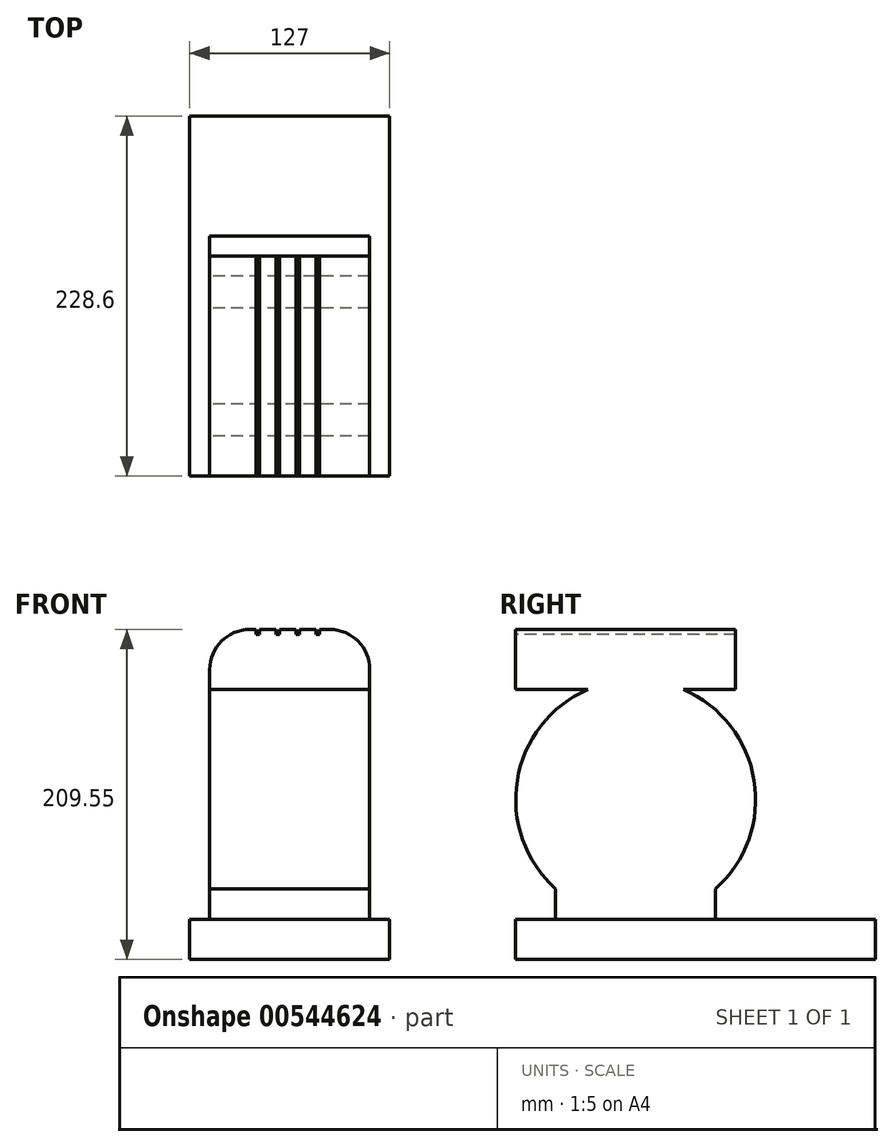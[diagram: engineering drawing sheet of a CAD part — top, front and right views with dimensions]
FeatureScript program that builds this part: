
annotation { "Feature Type Name" : "Feature", "Feature Type Description" : "" }
export const myFeature = defineFeature(function(context is Context, id is Id, definition is map)
    precondition{}
    {
        {
            var Q0;
            Q0=qCreatedBy(makeId("Right.planeOp"),FACE);
            var sketch = newSketch(context, id + "F0", { "sketchPlane" : qUnion([Q0])});
            skLineSegment(sketch, "E0.bottom", {"start": v(0, 0) * mm, "end": v(228.6, 0) * mm});
            skLineSegment(sketch, "E0.top", {"start": v(0, 25.4) * mm, "end": v(228.6, 25.4) * mm});
            skLineSegment(sketch, "E0.left", {"start": v(0, 0) * mm, "end": v(0, 25.4) * mm});
            skLineSegment(sketch, "E0.right", {"start": v(228.6, 0) * mm, "end": v(228.6, 25.4) * mm});
            skSolve(sketch);
        }
        {
            var Q0;
            Q0 = qSketchRegion(id + "F0", true);
            extrude(context, id + "F1", {"entities" : qUnion([Q0]), "endBound" : BoundingType.SYMMETRIC, "depth" : 127 * mm, "offsetDistance" : 25.4 * mm});
        }
        {
            var Q0;
            Q0=qCreatedBy(makeId("Right.planeOp"),FACE);
            var sketch = newSketch(context, id + "F2", { "sketchPlane" : qUnion([Q0])});
            skArc(sketch, "E1", {"start": v(127, 44.8) * mm, "mid": v(76.2, 177.8) * mm, "end": v(25.4, 44.8) * mm});
            skLineSegment(sketch, "E2", {"start": v(127, 44.8) * mm, "end": v(127, 6.35) * mm});
            skLineSegment(sketch, "E3", {"start": v(25.4, 44.8) * mm, "end": v(25.4, 6.35) * mm});
            skLineSegment(sketch, "E4", {"start": v(127, 6.35) * mm, "end": v(25.4, 6.35) * mm});
            skSolve(sketch);
        }
        {
            var Q0;
            Q0 = qSketchRegion(id + "F2", true);
            extrude(context, id + "F3", {"entities" : qUnion([Q0]), "operationType" : NewBodyOperationType.ADD, "endBound" : BoundingType.SYMMETRIC, "depth" : 101.6 * mm, "offsetDistance" : 25.4 * mm});
        }
        {
            var Q0;
            Q0=qCreatedBy(makeId("Front.planeOp"),FACE);
            var sketch = newSketch(context, id + "F4", { "sketchPlane" : qUnion([Q0])});
            skLineSegment(sketch, "E5", {"start": v(-50.8, 171.45) * mm, "end": v(50.8, 171.45) * mm});
            skLineSegment(sketch, "E6", {"start": v(0, 345.73) * mm, "end": v(0, 0) * mm, "construction": true});
            skLineSegment(sketch, "E7", {"start": v(-50.8, 171.45) * mm, "end": v(-50.8, 184.15) * mm});
            skLineSegment(sketch, "E8", {"start": v(50.8, 171.45) * mm, "end": v(50.8, 184.15) * mm});
            skLineSegment(sketch, "E9", {"start": v(-25.4, 209.55) * mm, "end": v(-21.57, 209.55) * mm});
            skPoint(sketch, "E10.visualSharp", {"position": v(-50.8, 209.55) * mm});
            skArc(sketch, "E10.filletArc", {"start": v(-25.4, 209.55) * mm, "mid": v(-43.36, 202.11) * mm, "end": v(-50.8, 184.15) * mm});
            skPoint(sketch, "E11.visualSharp", {"position": v(50.8, 209.55) * mm});
            skArc(sketch, "E11.filletArc", {"start": v(50.8, 184.15) * mm, "mid": v(43.36, 202.11) * mm, "end": v(25.4, 209.55) * mm});
            skLineSegment(sketch, "E12.top", {"start": v(18.87, 206.38) * mm, "end": v(16.53, 206.38) * mm});
            skLineSegment(sketch, "E12.left", {"start": v(18.87, 209.55) * mm, "end": v(18.87, 206.38) * mm});
            skLineSegment(sketch, "E12.right", {"start": v(16.53, 209.55) * mm, "end": v(16.53, 206.38) * mm});
            skLineSegment(sketch, "E13.top", {"start": v(6.17, 206.38) * mm, "end": v(3.83, 206.38) * mm});
            skLineSegment(sketch, "E13.left", {"start": v(6.17, 209.55) * mm, "end": v(6.17, 206.38) * mm});
            skLineSegment(sketch, "E13.right", {"start": v(3.83, 209.55) * mm, "end": v(3.83, 206.38) * mm});
            skLineSegment(sketch, "E14.top", {"start": v(-6.53, 206.38) * mm, "end": v(-8.87, 206.38) * mm});
            skLineSegment(sketch, "E14.left", {"start": v(-6.53, 209.55) * mm, "end": v(-6.53, 206.38) * mm});
            skLineSegment(sketch, "E14.right", {"start": v(-8.87, 209.55) * mm, "end": v(-8.87, 206.38) * mm});
            skLineSegment(sketch, "E15.top", {"start": v(-19.23, 206.38) * mm, "end": v(-21.57, 206.38) * mm});
            skLineSegment(sketch, "E15.left", {"start": v(-19.23, 209.55) * mm, "end": v(-19.23, 206.38) * mm});
            skLineSegment(sketch, "E15.right", {"start": v(-21.57, 209.55) * mm, "end": v(-21.57, 206.38) * mm});
            skLineSegment(sketch, "E16.trimOffspring", {"start": v(18.87, 209.55) * mm, "end": v(25.4, 209.55) * mm});
            skLineSegment(sketch, "E17.trimOffspring", {"start": v(6.17, 209.55) * mm, "end": v(16.53, 209.55) * mm});
            skLineSegment(sketch, "E18.trimOffspring", {"start": v(-6.53, 209.55) * mm, "end": v(3.83, 209.55) * mm});
            skLineSegment(sketch, "E19.trimOffspring", {"start": v(-19.23, 209.55) * mm, "end": v(-8.87, 209.55) * mm});
            skSolve(sketch);
        }
        {
            var Q0;
            Q0=makeQuery(id+"F4.imprint","IMPRINT",FACE,{"disambiguationData":[TD([[makeQuery(id+"F4.imprint","IMPRINT",EDGE,{"derivedFrom":sQuery(id+"F4.wireOp",EDGE,"E5")}),1.0]])]});
            extrude(context, id + "F5", {"entities" : qUnion([Q0]), "operationType" : NewBodyOperationType.ADD, "oppositeDirection" : true, "depth" : 139.7 * mm, "offsetDistance" : 25.4 * mm});
        }
    });
